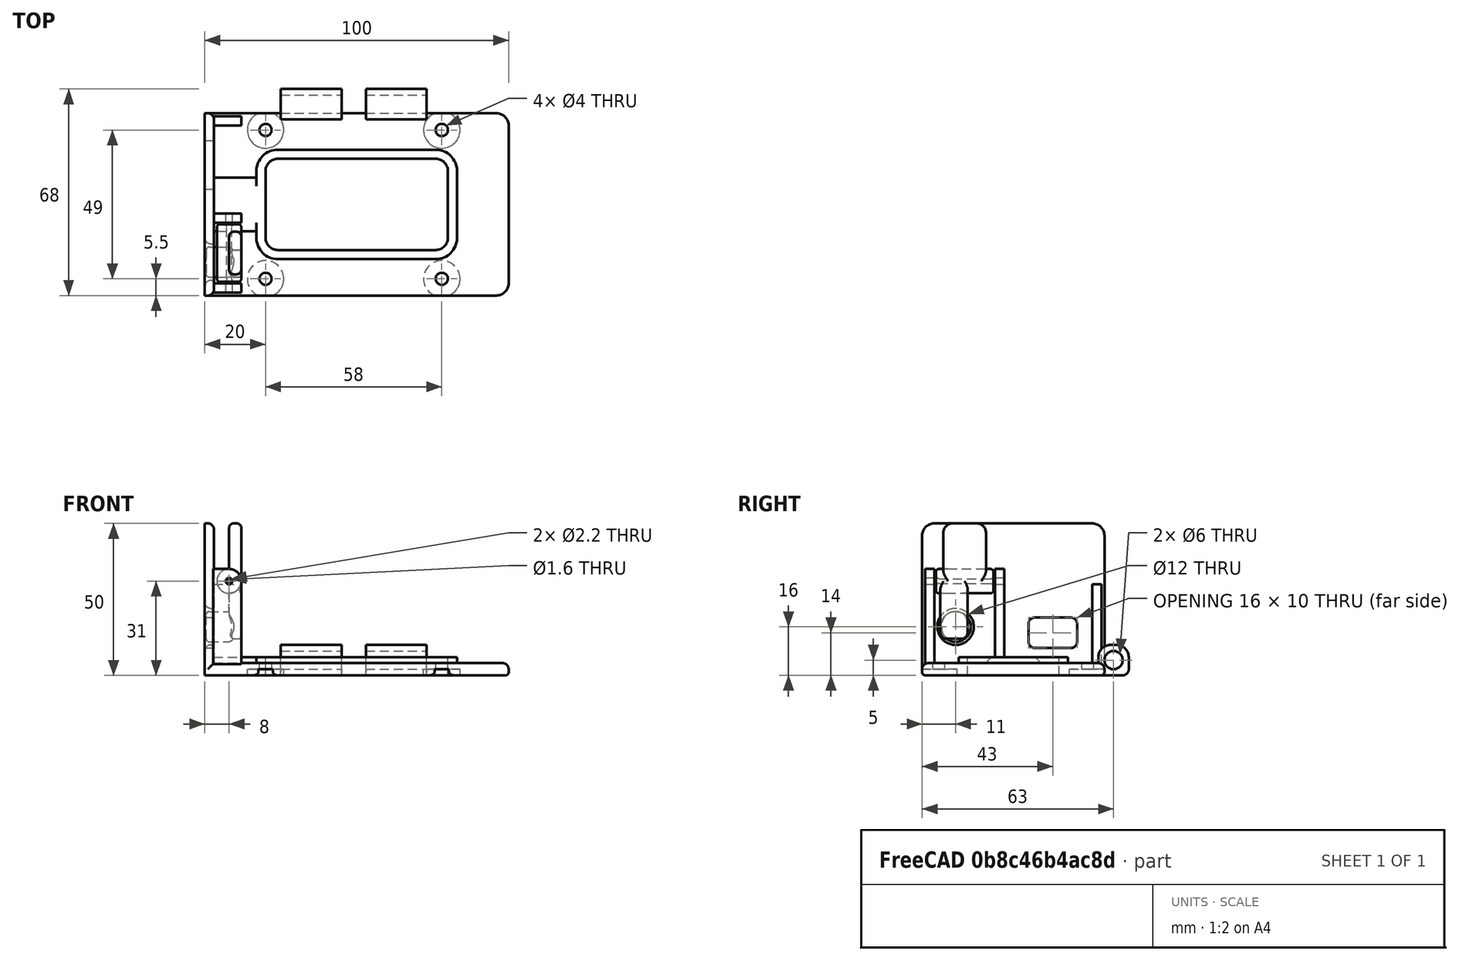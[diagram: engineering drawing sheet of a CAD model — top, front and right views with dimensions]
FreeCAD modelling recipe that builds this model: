
FCSTD DOCUMENT  (FreeCAD 0.19R)
Label: OPI5_Pro_Case
License: All rights reserved
LicenseURL: http://en.wikipedia.org/wiki/All_rights_reserved
objects: Part::Fillet×24, Part::Cylinder×15, Part::Box×12, Part::MultiFuse×7, Part::Cut×6, Part::Feature×1, Part::Chamfer×1
note: 66 computed .brp shape members not serialized (recipe doc carries the construction recipe); baked Part::Feature solids carry a one-line shape summary decoded from their .brp

FEATURE [Part::Cylinder] Cylinder  label="ScrewHolle001"
  Angle = 360
  AttacherType = Attacher::AttachEngine3D
  Height = 10
  Placement = pos=(0,-24.5,0) rot=(0,0,1;0rad)
  Radius = 2
FEATURE [Part::Cylinder] Cylinder001  label="ScrewHolle002"
  Angle = 360
  AttacherType = Attacher::AttachEngine3D
  Height = 10
  Placement = pos=(0,24.5,0) rot=(0,0,1;0rad)
  Radius = 2
FEATURE [Part::Cylinder] Cylinder002  label="ScrewHolle003"
  Angle = 360
  AttacherType = Attacher::AttachEngine3D
  Height = 10
  Placement = pos=(58,-24.5,0) rot=(0,0,1;0rad)
  Radius = 2
FEATURE [Part::Cylinder] Cylinder003  label="ScrewHolle004"
  Angle = 360
  AttacherType = Attacher::AttachEngine3D
  Height = 10
  Placement = pos=(58,24.5,0) rot=(0,0,1;0rad)
  Radius = 2
FEATURE [Part::Cylinder] Cylinder004  label="ScrewHolle005"
  Angle = 360
  AttacherType = Attacher::AttachEngine3D
  Height = 2
  Placement = pos=(0,-24.5,0) rot=(0,0,1;0rad)
  Radius = 6
FEATURE [Part::Cylinder] Cylinder005  label="ScrewHolle006"
  Angle = 360
  AttacherType = Attacher::AttachEngine3D
  Height = 2
  Placement = pos=(0,24.5,0) rot=(0,0,1;0rad)
  Radius = 6
FEATURE [Part::Cylinder] Cylinder006  label="ScrewHolle007"
  Angle = 360
  AttacherType = Attacher::AttachEngine3D
  Height = 2
  Placement = pos=(58,24.5,0) rot=(0,0,1;0rad)
  Radius = 6
FEATURE [Part::Cylinder] Cylinder007  label="ScrewHolle008"
  Angle = 360
  AttacherType = Attacher::AttachEngine3D
  Height = 2
  Placement = pos=(58,-24.5,0) rot=(0,0,1;0rad)
  Radius = 6
FEATURE [Part::MultiFuse] Fusion  label="ScrewHolles"
  Shapes = -> [Cylinder,Cylinder001,Cylinder002,Cylinder003,Cylinder004,Cylinder005,Cylinder006,Cylinder007]
FEATURE [Part::Box] Box  label="Cube"
  AttacherType = Attacher::AttachEngine3D
  Height = 4
  Length = 100
  Placement = pos=(-20,-30,0) rot=(0,0,1;0rad)
  Width = 60
FEATURE [Part::Box] Box001  label="Cube001"
  AttacherType = Attacher::AttachEngine3D
  Height = 49
  Length = 3
  Placement = pos=(-20,-30,1) rot=(0,0,1;0rad)
  Width = 60
FEATURE [Part::Box] Box003  label="Cube003"
  AttacherType = Attacher::AttachEngine3D
  Height = 19
  Length = 4
  Placement = pos=(-12,-24,12) rot=(0,0,1;0rad)
  Width = 9
FEATURE [Part::Cylinder] Cylinder009
  Angle = 360
  AttacherType = Attacher::AttachEngine3D
  Height = 19
  Placement = pos=(-12,-25.5,31) rot=(-1,0,0;1.5708rad)
  Radius = 4
FEATURE [Part::Fillet] Fillet
  Base = -> Box003
  Edges = 2 edges r=2: [Edge9,Edge11]
FEATURE [Part::Fillet] Fillet001
  Base = -> Fillet
  Edges = 1 edges r=2: [Edge5]
FEATURE [Part::Fillet] Fillet002
  Base = -> Fillet001
  Edges = 1 edges r=1: [Edge20]
FEATURE [Part::Box] Box004  label="Cube004"
  AttacherType = Attacher::AttachEngine3D
  Height = 19
  Length = 4
  Placement = pos=(-12,-23,31) rot=(0,0,1;0rad)
  Width = 14
FEATURE [Part::Fillet] Fillet003
  Base = -> Box004
  Edges = 2 edges r=3: [Edge10,Edge12]
FEATURE [Part::Fillet] Fillet004
  Base = -> Fillet003
  Edges = 1 edges r=1.5: [Edge1]
FEATURE [Part::Fillet] Fillet005
  Base = -> Fillet004
  Edges = 1 edges r=1.5: [Edge22]
FEATURE [Part::MultiFuse] Fusion002  label="Key"
  Shapes = -> [Fillet005,Cylinder009,Fillet002]
FEATURE [Part::Cylinder] Cylinder010
  Angle = 360
  AttacherType = Attacher::AttachEngine3D
  Height = 20
  Placement = pos=(-12,-26,31) rot=(-1,0,0;1.5708rad)
  Radius = 0.8
FEATURE [Part::Cut] Cut
  Base = -> Fusion002
  Tool = -> Cylinder010
FEATURE [Part::Fillet] Fillet006  label="PushButtonMain"
  Base = -> Cut
  Edges = 4 edges r=1: [Edge11,Edge20,Edge44,Edge61]
FEATURE [Part::Fillet] Fillet007
  Base = -> Box
  Edges = 2 edges r=4: [Edge5,Edge7]
FEATURE [Part::Box] Box005  label="Cube005"
  AttacherType = Attacher::AttachEngine3D
  Height = 35
  Length = 12
  Placement = pos=(-20,-29,0) rot=(0,0,1;0rad)
  Width = 3
FEATURE [Part::Box] Box006  label="Cube006"
  AttacherType = Attacher::AttachEngine3D
  Height = 35
  Length = 12
  Placement = pos=(-20,-6,0) rot=(0,0,1;0rad)
  Width = 3
FEATURE [Part::Fillet] Fillet008
  Base = -> Box005
  Edges = 1 edges r=4: [Edge6]
FEATURE [Part::Fillet] Fillet009
  Base = -> Box006
  Edges = 1 edges r=4: [Edge6]
FEATURE [Part::Cylinder] Cylinder011
  Angle = 360
  AttacherType = Attacher::AttachEngine3D
  Height = 40
  Placement = pos=(-12,-30,31) rot=(-1,0,0;1.5708rad)
  Radius = 1.1
FEATURE [Part::Cut] Cut001
  Base = -> Fillet008
  Tool = -> Cylinder011
FEATURE [Part::Cylinder] Cylinder012
  Angle = 360
  AttacherType = Attacher::AttachEngine3D
  Height = 40
  Placement = pos=(-12,-30,31) rot=(-1,0,0;1.5708rad)
  Radius = 1.1
FEATURE [Part::Cut] Cut002
  Base = -> Fillet009
  Tool = -> Cylinder012
FEATURE [Part::Fillet] Fillet010
  Base = -> Box001
  Edges = 2 edges r=4: [Edge10,Edge12]
FEATURE [Part::Fillet] Fillet011
  Base = -> Fillet010
  Edges = 1 edges r=2: [Edge16]
FEATURE [Part::Fillet] Fillet012
  Base = -> Fillet007
  Edges = 1 edges r=2: [Edge5]
FEATURE [Part::Fillet] Fillet013
  Base = -> Fillet012
  Edges = 1 edges r=1: [Edge11]
FEATURE [Part::Box] Box007  label="Cube007"
  AttacherType = Attacher::AttachEngine3D
  Height = 10
  Length = 10
  Placement = pos=(-20,5,9) rot=(0,0,1;0rad)
  Width = 16
FEATURE [Part::Fillet] Fillet014  label="SIM_Holle"
  Base = -> Box007
  Edges = 4 edges r=2: [Edge9,Edge10,Edge11,Edge12]
FEATURE [Part::Box] Box008  label="Cube008"
  AttacherType = Attacher::AttachEngine3D
  Height = 30
  Length = 12
  Placement = pos=(-20,-6,0) rot=(0,0,1;0rad)
  Width = 3
FEATURE [Part::Fillet] Fillet015
  Base = -> Box008
  Edges = 1 edges r=4: [Edge6]
  Placement = pos=(0,32,0) rot=(0,0,1;0rad)
FEATURE [Part::Box] Box009  label="Cube009"
  AttacherType = Attacher::AttachEngine3D
  Height = 6
  Length = 60
  Placement = pos=(0,-15,0) rot=(0,0,1;0rad)
  Width = 30
FEATURE [Part::Fillet] Fillet016
  Base = -> Box009
  Edges = 4 edges r=4: [Edge1,Edge3,Edge5,Edge7]
FEATURE [Part::Box] Box010  label="Cube010"
  AttacherType = Attacher::AttachEngine3D
  Height = 6
  Length = 66
  Placement = pos=(-3,-18,0) rot=(0,0,1;0rad)
  Width = 36
FEATURE [Part::Fillet] Fillet017
  Base = -> Box010
  Edges = 4 edges r=7: [Edge1,Edge3,Edge5,Edge7]
FEATURE [Part::MultiFuse] Fusion003
  Shapes = -> [Fillet013,Fillet017]
FEATURE [Part::MultiFuse] Fusion004
  Shapes = -> [Fillet016,Fusion]
FEATURE [Part::Cut] Cut004
  Base = -> Fusion003
  Tool = -> Fusion004
FEATURE [Part::Box] Box011  label="Cube011"
  AttacherType = Attacher::AttachEngine3D
  Height = 6
  Length = 20
  Placement = pos=(-20,-9,0) rot=(0,0,1;0rad)
  Width = 18
FEATURE [Part::Fillet] Fillet018
  Base = -> Box011
  Edges = 2 edges r=3: [Edge10,Edge12]
FEATURE [Part::Box] Box012  label="Cube012"
  AttacherType = Attacher::AttachEngine3D
  Height = 10
  Length = 20
  Placement = pos=(5,28,0) rot=(0,0,1;0rad)
  Width = 10
FEATURE [Part::Fillet] Fillet019
  Base = -> Box012
  Edges = 2 edges r=4: [Edge10,Edge12]
FEATURE [Part::Fillet] Fillet020
  Base = -> Fillet019
  Edges = 1 edges r=2: [Edge12]
FEATURE [Part::Cylinder] Cylinder013  label="Cylinder"
  Angle = 360
  AttacherType = Attacher::AttachEngine3D
  Height = 60
  Placement = pos=(0,33,5) rot=(0,1,0;1.5708rad)
  Radius = 3
FEATURE [Part::Cut] Cut005  label="AntennaHolder"
  Base = -> Fillet020
  Tool = -> Cylinder013
FEATURE [Part::Feature] Cut005001  label="AntennaHolder001"
  Placement = pos=(28,0,0) rot=(0,0,1;0rad)
  shape: bbox 20 x 10 x 10 mm, 10 faces (baked)
FEATURE [Part::Cylinder] Cylinder014  label="ButtonHolle"
  Angle = 360
  AttacherType = Attacher::AttachEngine3D
  Height = 10
  Placement = pos=(-20,-19,16) rot=(0,1,0;1.5708rad)
  Radius = 6
FEATURE [Part::MultiFuse] Fusion005
  Shapes = -> [Fillet014,Cylinder014]
FEATURE [Part::Cut] Cut005002
  Base = -> Fillet011
  Tool = -> Fusion005
FEATURE [Part::MultiFuse] Fusion006  label="OPI5_Holder_body"
  Shapes = -> [Cut001,Cut002,Fillet015,Cut004,Fillet018,Cut005,Cut005001,Cut005002]
FEATURE [Part::Fillet] Fillet021  label="OPI5_Holder"
  Base = -> Fusion006
  Edges = 1 edges r=2: [Edge272]
FEATURE [Part::Cylinder] Cylinder015  label="Button"
  Angle = 360
  AttacherType = Attacher::AttachEngine3D
  Height = 10
  Placement = pos=(-19.5,-19,16) rot=(0,1,0;1.5708rad)
  Radius = 5
FEATURE [Part::Fillet] Fillet022
  Base = -> Cylinder015
  Edges = 1 edges r=1: [Edge3]
FEATURE [Part::Chamfer] Chamfer
  Base = -> Fillet022
  Edges = 1 edges r=2: [Edge2]
FEATURE [Part::Fillet] Fillet023
  Base = -> Chamfer
  Edges = 1 edges r=3: [Edge2]
FEATURE [Part::MultiFuse] Fusion007  label="PushButton"
  Shapes = -> [Fillet006,Fillet023]
